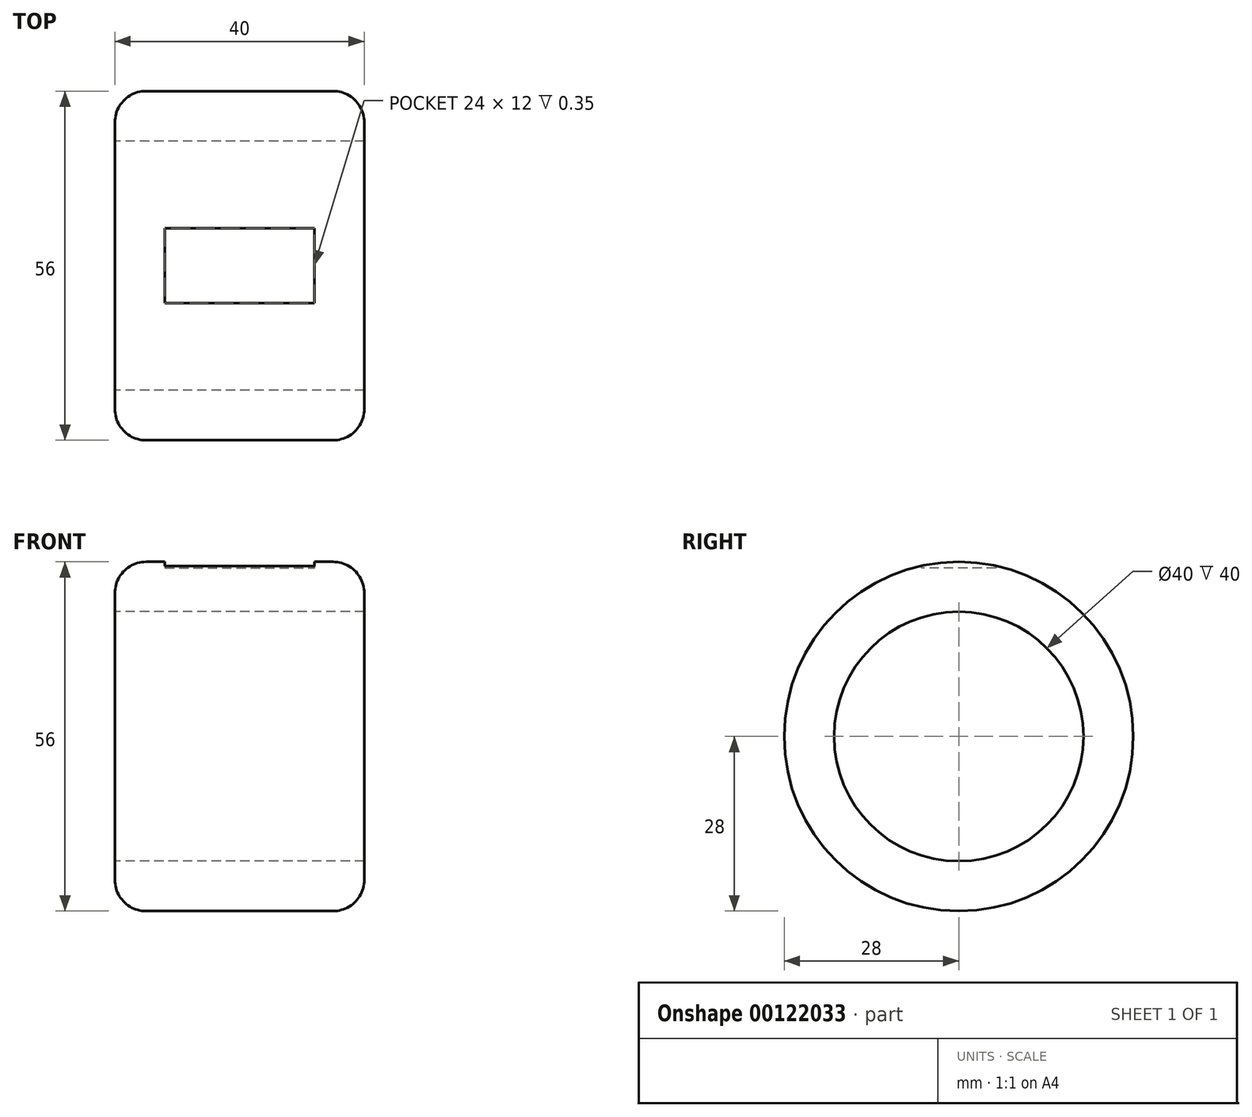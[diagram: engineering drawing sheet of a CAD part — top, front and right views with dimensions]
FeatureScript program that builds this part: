
annotation { "Feature Type Name" : "Feature", "Feature Type Description" : "" }
export const myFeature = defineFeature(function(context is Context, id is Id, definition is map)
    precondition{}
    {
        {
            var Q0;
            Q0=qCreatedBy(makeId("Front.planeOp"),FACE);
            var sketch = newSketch(context, id + "F0", { "sketchPlane" : qUnion([Q0])});
            skLineSegment(sketch, "E0", {"start": v(-20.94, 0) * mm, "end": v(26.48, 0) * mm});
            skLineSegment(sketch, "E1", {"start": v(0, 24) * mm, "end": v(0, 0) * mm});
            skLineSegment(sketch, "E2.bottom", {"start": v(-20, 20) * mm, "end": v(20, 20) * mm});
            skLineSegment(sketch, "E2.top", {"start": v(-20, 28) * mm, "end": v(20, 28) * mm});
            skLineSegment(sketch, "E2.left", {"start": v(-20, 20) * mm, "end": v(-20, 28) * mm});
            skLineSegment(sketch, "E2.right", {"start": v(20, 20) * mm, "end": v(20, 28) * mm});
            skPoint(sketch, "E2.middle", {"position": v(0, 24) * mm});
            skLineSegment(sketch, "E3.bottom", {"start": v(-12, 29) * mm, "end": v(12, 29) * mm});
            skLineSegment(sketch, "E3.top", {"start": v(-12, 27) * mm, "end": v(12, 27) * mm});
            skLineSegment(sketch, "E3.left", {"start": v(-12, 29) * mm, "end": v(-12, 27) * mm});
            skLineSegment(sketch, "E3.right", {"start": v(12, 29) * mm, "end": v(12, 27) * mm});
            skPoint(sketch, "E3.middle", {"position": v(0, 28) * mm});
            skSolve(sketch);
        }
        {
            var Q0;
            Q0=makeQuery(id+"F0.imprint","IMPRINT",FACE,{"disambiguationData":[TD([[makeQuery(id+"F0.imprint","IMPRINT",EDGE,{"derivedFrom":sQuery(id+"F0.wireOp",EDGE,"E2.top")}),-1.0]])]});
            var Q1;
            {var subQ5=sQuery(id+"F0.wireOp",EDGE,"E3.top");Q1=makeQuery(id+"F0.imprint","IMPRINT",FACE,{"disambiguationData":[TD([[makeQuery(id+"F0.imprint","IMPRINT",EDGE,{"derivedFrom":subQ5}),1.0]])]});}
            var Q2;
            Q2=sQuery(id+"F0.wireOp",EDGE,"E0");
            revolve(context, id + "F1", {"entities" : qUnion([Q0, Q1]), "axis" : qUnion([Q2]), "revolveType" : RevolveType.FULL});
        }
        {
            var Q0;
            Q0=makeQuery(id+"F1.opRevolve","SWEPT_EDGE",EDGE,{"disambiguationData":[OSD([sQuery(id+"F0.wireOp",EDGE,"E2.top"),sQuery(id+"F0.wireOp",EDGE,"E2.right")])]});
            var Q1;
            Q1=makeQuery(id+"F1.opRevolve","SWEPT_EDGE",EDGE,{"disambiguationData":[OSD([sQuery(id+"F0.wireOp",EDGE,"E2.top"),sQuery(id+"F0.wireOp",EDGE,"E2.left")])]});
            fillet(context, id + "F2", {"entities" : qUnion([Q0, Q1]), "radius" : 5 * mm, "tangentPropagation" : true, "allowEdgeOverflow" : false});
        }
        {
            var Q0;
            {var subQ5=sQuery(id+"F0.wireOp",EDGE,"E3.top");Q0=makeQuery(id+"F0.imprint","IMPRINT",FACE,{"disambiguationData":[TD([[makeQuery(id+"F0.imprint","IMPRINT",EDGE,{"derivedFrom":subQ5}),1.0]])]});}
            extrude(context, id + "F3", {"entities" : qUnion([Q0]), "operationType" : NewBodyOperationType.REMOVE, "endBound" : BoundingType.SYMMETRIC, "oppositeDirection" : true, "depth" : 12 * mm});
        }
    });
